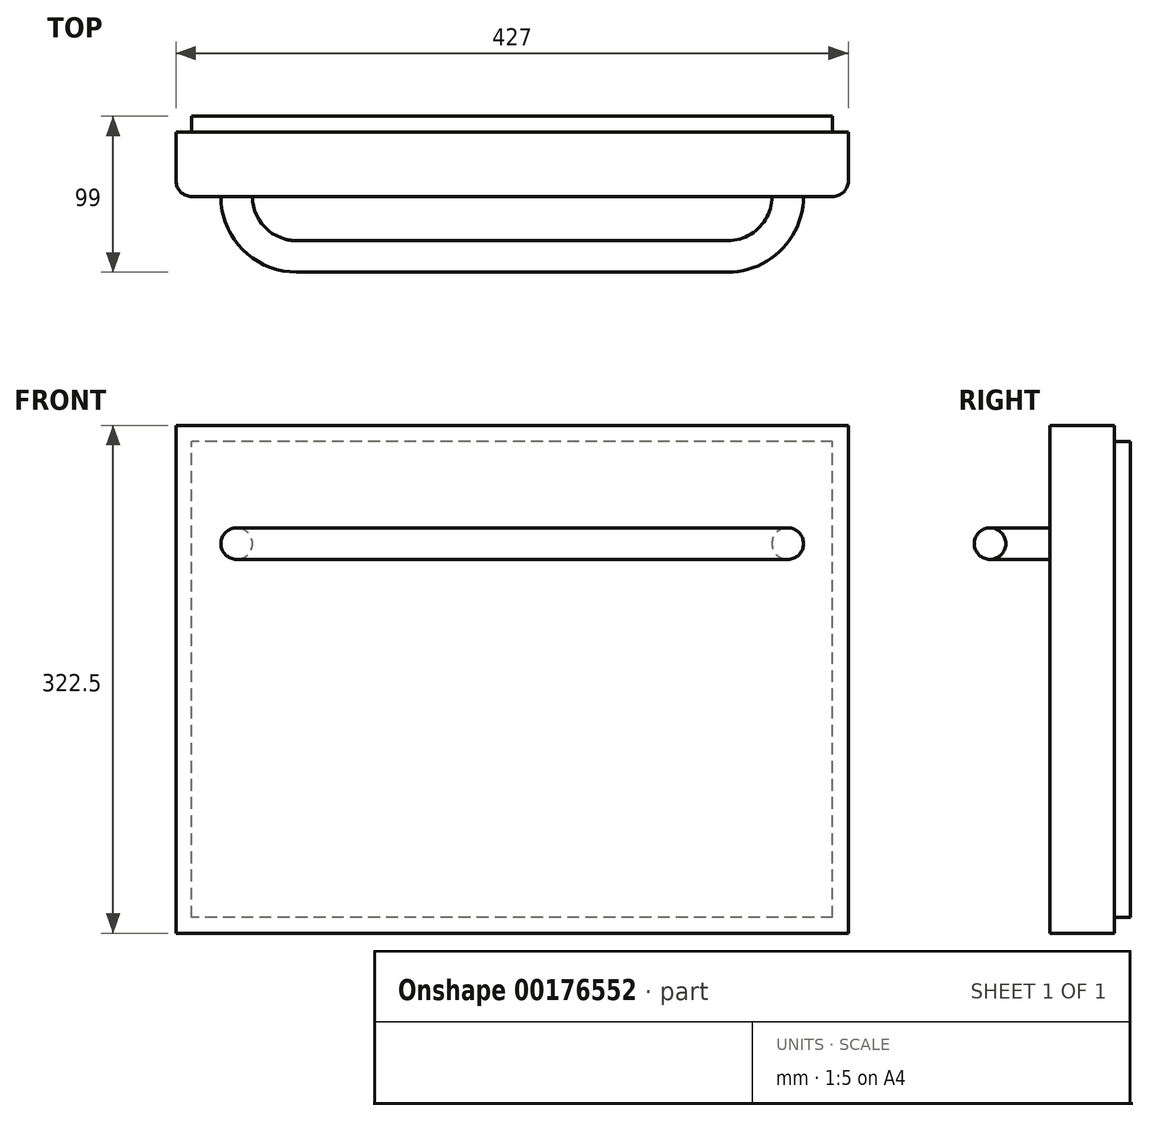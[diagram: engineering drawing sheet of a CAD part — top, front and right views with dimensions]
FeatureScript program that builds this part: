
annotation { "Feature Type Name" : "Feature", "Feature Type Description" : "" }
export const myFeature = defineFeature(function(context is Context, id is Id, definition is map)
    precondition{}
    {
        {
            var Q0;
            Q0=qCreatedBy(makeId("Front.planeOp"),FACE);
            var sketch = newSketch(context, id + "F0", { "sketchPlane" : qUnion([Q0])});
            skLineSegment(sketch, "E0.bottom", {"start": v(213.5, 161.25) * mm, "end": v(-213.5, 161.25) * mm});
            skLineSegment(sketch, "E0.top", {"start": v(213.5, -161.25) * mm, "end": v(-213.5, -161.25) * mm});
            skLineSegment(sketch, "E0.left", {"start": v(213.5, 161.25) * mm, "end": v(213.5, -161.25) * mm});
            skLineSegment(sketch, "E0.right", {"start": v(-213.5, 161.25) * mm, "end": v(-213.5, -161.25) * mm});
            skPoint(sketch, "E0.middle", {"position": v(0, 0) * mm});
            skSolve(sketch);
        }
        {
            var Q0;
            Q0 = qSketchRegion(id + "F0", true);
            extrude(context, id + "F1", {"entities" : qUnion([Q0]), "depth" : 41 * mm});
        }
        {
            var Q0;
            Q0=makeQuery(id+"F1.opExtrude","CAP_EDGE",EDGE,{"disambiguationData":[OSD([sQuery(id+"F0.wireOp",EDGE,"E0.right")])],"isStart":false});
            var Q1;
            Q1=makeQuery(id+"F1.opExtrude","CAP_EDGE",EDGE,{"disambiguationData":[OSD([sQuery(id+"F0.wireOp",EDGE,"E0.left")])],"isStart":false});
            fillet(context, id + "F2", {"entities" : qUnion([Q0, Q1]), "radius" : 10 * mm, "tangentPropagation" : true, "allowEdgeOverflow" : false});
        }
        {
            var Q0;
            Q0=makeQuery(id+"F1.opExtrude","CAP_FACE",FACE,{"disambiguationData":[OSD([sQuery(id+"F0.wireOp",EDGE,"E0.bottom"),sQuery(id+"F0.wireOp",EDGE,"E0.top"),sQuery(id+"F0.wireOp",EDGE,"E0.left"),sQuery(id+"F0.wireOp",EDGE,"E0.right")])],"isStart":true});
            var sketch = newSketch(context, id + "F3", { "sketchPlane" : qUnion([Q0])});
            skLineSegment(sketch, "E1.bottom", {"start": v(-203.5, -151.25) * mm, "end": v(203.5, -151.25) * mm});
            skLineSegment(sketch, "E1.top", {"start": v(-203.5, 151.25) * mm, "end": v(203.5, 151.25) * mm});
            skLineSegment(sketch, "E1.left", {"start": v(-203.5, -151.25) * mm, "end": v(-203.5, 151.25) * mm});
            skLineSegment(sketch, "E1.right", {"start": v(203.5, -151.25) * mm, "end": v(203.5, 151.25) * mm});
            skSolve(sketch);
        }
        {
            var Q0;
            Q0 = qSketchRegion(id + "F3", true);
            extrude(context, id + "F4", {"entities" : qUnion([Q0]), "depth" : 10 * mm});
        }
        {
            var Q0;
            Q0=makeQuery(id+"F1.opExtrude","CAP_FACE",FACE,{"disambiguationData":[OSD([sQuery(id+"F0.wireOp",EDGE,"E0.bottom"),sQuery(id+"F0.wireOp",EDGE,"E0.top"),sQuery(id+"F0.wireOp",EDGE,"E0.left"),sQuery(id+"F0.wireOp",EDGE,"E0.right")])],"isStart":false});
            var sketch = newSketch(context, id + "F5", { "sketchPlane" : qUnion([Q0])});
            skCircle(sketch, "E2", {"center": v(-175, 86.25) * mm, "radius": 10 * mm});
            skSolve(sketch);
        }
        {
            var Q0;
            Q0=makeQuery(id+"F1.opExtrude","SWEPT_FACE",FACE,{"disambiguationData":[OSD([sQuery(id+"F0.wireOp",EDGE,"E0.bottom")])]});
            cPlane(context, id + "F6", {"entities" : qUnion([Q0]), "cplaneType" : CPlaneType.OFFSET, "offset" : 75 * mm, "oppositeDirection" : true, "width" : 150 * mm, "height" : 150 * mm});
        }
        {
            var Q0;
            Q0=qCreatedBy(id+"F6.planeOp",FACE);
            var sketch = newSketch(context, id + "F7", { "sketchPlane" : qUnion([Q0])});
            skLineSegment(sketch, "E3", {"start": v(-175, -41) * mm, "end": v(-175, -41) * mm});
            skLineSegment(sketch, "E4", {"start": v(-137, -79) * mm, "end": v(137, -79) * mm});
            skLineSegment(sketch, "E5", {"start": v(175, -41) * mm, "end": v(175, -41) * mm});
            skPoint(sketch, "E6.visualSharp", {"position": v(-175, -79) * mm});
            skArc(sketch, "E6.filletArc", {"start": v(-175, -41) * mm, "mid": v(-163.87, -67.87) * mm, "end": v(-137, -79) * mm});
            skPoint(sketch, "E7.visualSharp", {"position": v(175, -79) * mm});
            skArc(sketch, "E7.filletArc", {"start": v(137, -79) * mm, "mid": v(163.87, -67.87) * mm, "end": v(175, -41) * mm});
            skSolve(sketch);
        }
        {
            var Q0;
            Q0=makeQuery(id+"F5.imprint","IMPRINT",FACE,{"disambiguationData":[TD([[makeQuery(id+"F5.imprint","IMPRINT",EDGE,{"derivedFrom":sQuery(id+"F5.wireOp",EDGE,"E2")}),1.0]])]});
            var Q1;
            Q1=sQuery(id+"F7.wireOp",EDGE,"E6.filletArc");
            var Q2;
            Q2=sQuery(id+"F7.wireOp",EDGE,"E4");
            var Q3;
            Q3=sQuery(id+"F7.wireOp",EDGE,"E7.filletArc");
            sweep(context, id + "F8", {"operationType" : NewBodyOperationType.ADD, "profiles" : qUnion([Q0]), "path" : qUnion([Q1, Q2, Q3])});
        }
    });
